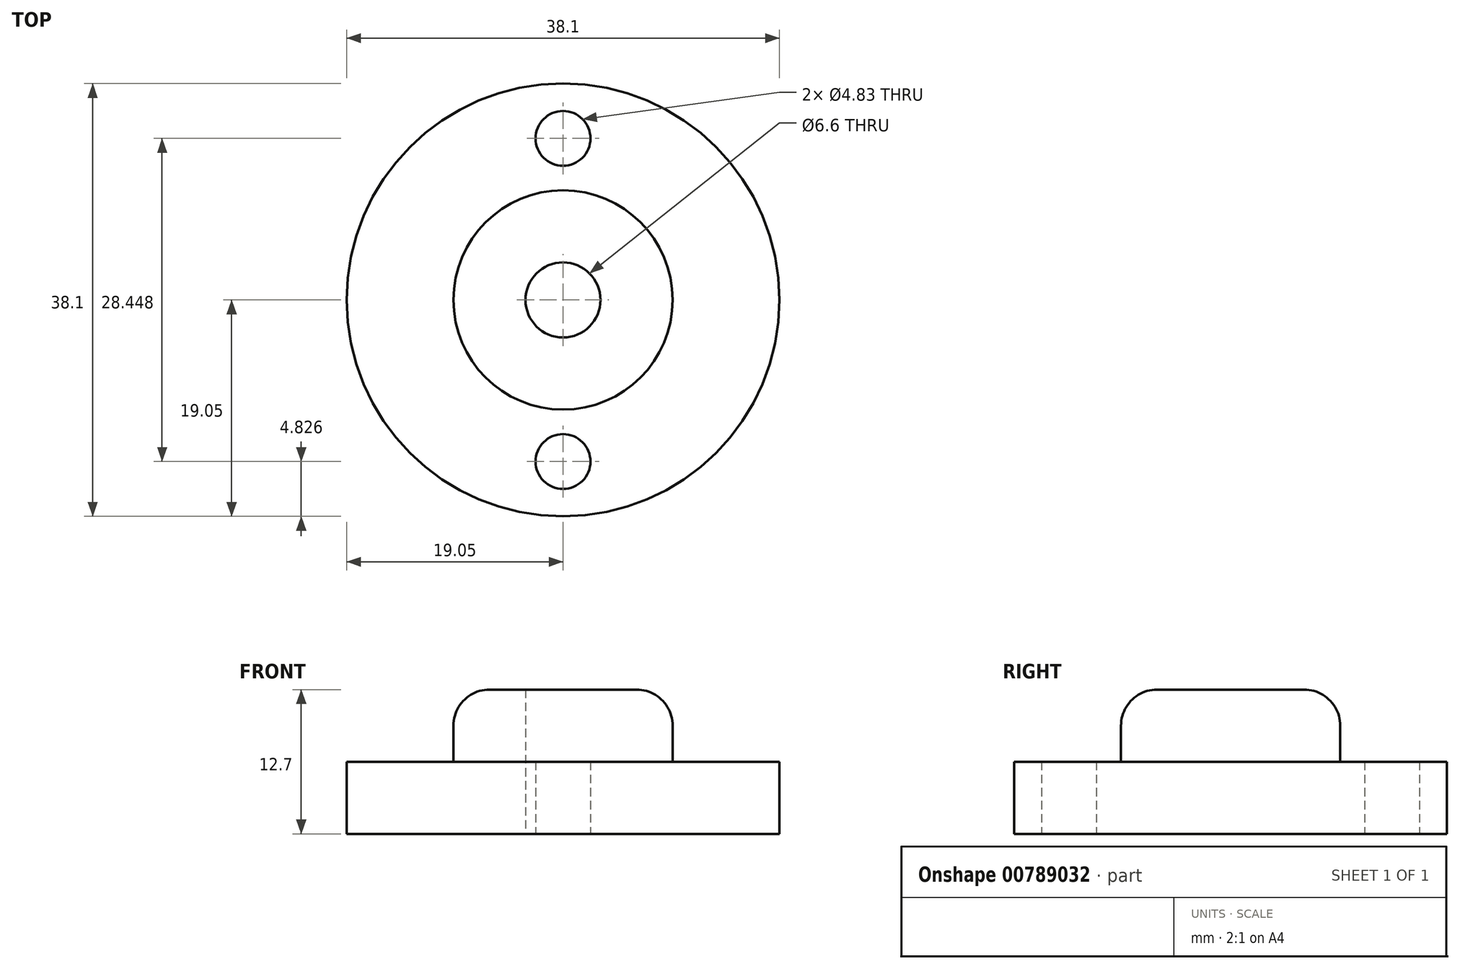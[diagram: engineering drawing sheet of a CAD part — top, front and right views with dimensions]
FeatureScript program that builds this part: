
annotation { "Feature Type Name" : "Feature", "Feature Type Description" : "" }
export const myFeature = defineFeature(function(context is Context, id is Id, definition is map)
    precondition{}
    {
        {
            var Q0;
            Q0=qCreatedBy(makeId("Front.planeOp"),FACE);
            var sketch = newSketch(context, id + "F0", { "sketchPlane" : qUnion([Q0])});
            skLineSegment(sketch, "E0", {"start": v(0, -23.33) * mm, "end": v(0, 52.87) * mm, "construction": true});
            skLineSegment(sketch, "E1", {"start": v(-3.3, 0) * mm, "end": v(-19.05, 0) * mm});
            skLineSegment(sketch, "E2", {"start": v(-19.05, 0) * mm, "end": v(-19.05, 6.35) * mm});
            skLineSegment(sketch, "E3", {"start": v(-19.05, 6.35) * mm, "end": v(-9.65, 6.35) * mm});
            skLineSegment(sketch, "E4", {"start": v(-9.65, 6.35) * mm, "end": v(-9.65, 12.7) * mm});
            skLineSegment(sketch, "E5", {"start": v(-9.65, 12.7) * mm, "end": v(-3.3, 12.7) * mm});
            skLineSegment(sketch, "E6", {"start": v(-3.3, 12.7) * mm, "end": v(-3.3, 0) * mm});
            skSolve(sketch);
        }
        {
            var Q0;
            Q0 = qSketchRegion(id + "F0", true);
            var Q1;
            Q1=sQuery(id+"F0.wireOp",EDGE,"E0");
            revolve(context, id + "F1", {"surfaceOperationType" : NewSurfaceOperationType.NEW, "entities" : qUnion([Q0]), "axis" : qUnion([Q1]), "revolveType" : RevolveType.FULL});
        }
        {
            var Q0;
            Q0=makeQuery(id+"F1.opRevolve","SWEPT_FACE",FACE,{"disambiguationData":[OSD([sQuery(id+"F0.wireOp",EDGE,"E1")])]});
            var sketch = newSketch(context, id + "F2", { "sketchPlane" : qUnion([Q0])});
            skCircle(sketch, "E7", {"center": v(0, -14.22) * mm, "radius": 2.41 * mm});
            skCircle(sketch, "E8", {"center": v(0, 14.22) * mm, "radius": 2.41 * mm});
            skSolve(sketch);
        }
        {
            var Q0;
            Q0=makeQuery(id+"F2.imprint","IMPRINT",FACE,{"disambiguationData":[TD([[makeQuery(id+"F2.imprint","IMPRINT",EDGE,{"derivedFrom":sQuery(id+"F2.wireOp",EDGE,"E7")}),1.0]])]});
            var Q1;
            Q1=makeQuery(id+"F2.imprint","IMPRINT",FACE,{"disambiguationData":[TD([[makeQuery(id+"F2.imprint","IMPRINT",EDGE,{"derivedFrom":sQuery(id+"F2.wireOp",EDGE,"E8")}),1.0]])]});
            extrude(context, id + "F3", {"entities" : qUnion([Q0, Q1]), "operationType" : NewBodyOperationType.REMOVE, "oppositeDirection" : true, "depth" : 25.4 * mm, "offsetDistance" : 25.4 * mm});
        }
        {
            var Q0;
            Q0=makeQuery(id+"F1.opRevolve","SWEPT_EDGE",EDGE,{"disambiguationData":[OSD([sQuery(id+"F0.wireOp",EDGE,"E4"),sQuery(id+"F0.wireOp",EDGE,"E5")])]});
            fillet(context, id + "F4", {"entities" : qUnion([Q0]), "radius" : 3.17 * mm, "tangentPropagation" : true, "allowEdgeOverflow" : false});
        }
    });
